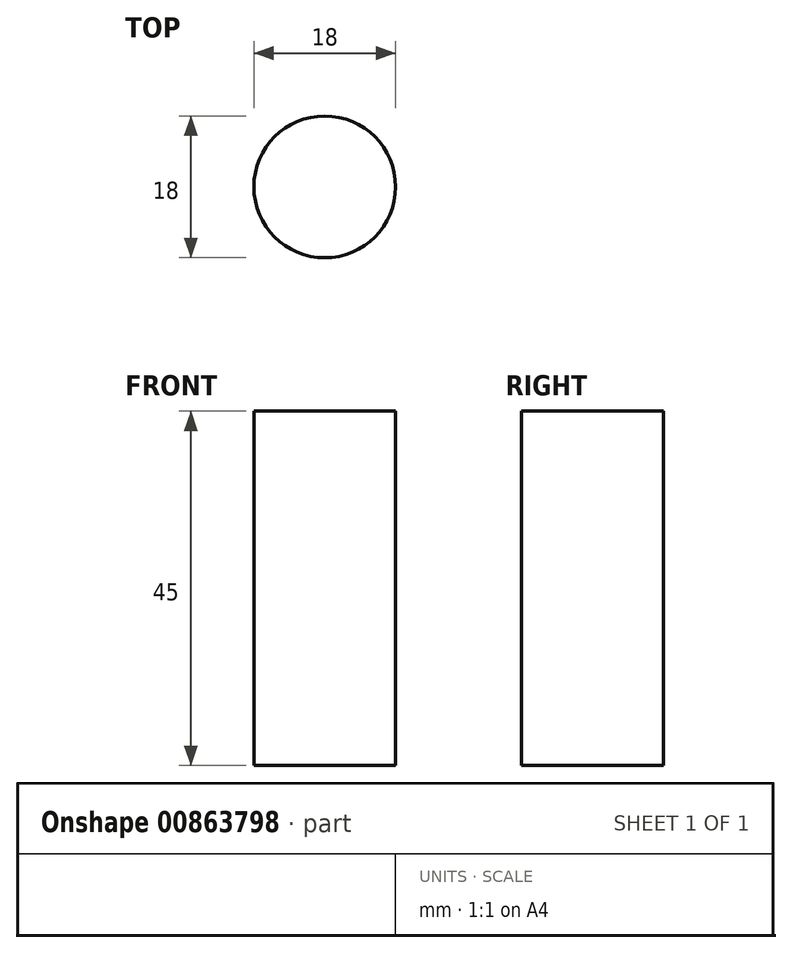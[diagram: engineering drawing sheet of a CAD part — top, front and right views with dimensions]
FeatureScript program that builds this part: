
annotation { "Feature Type Name" : "Feature", "Feature Type Description" : "" }
export const myFeature = defineFeature(function(context is Context, id is Id, definition is map)
    precondition{}
    {
        {
            var Q0;
            Q0=qCreatedBy(makeId("Top.planeOp"),FACE);
            var sketch = newSketch(context, id + "F0", { "sketchPlane" : qUnion([Q0])});
            skCircle(sketch, "E0", {"center": v(0, 0) * mm, "radius": 9 * mm});
            skSolve(sketch);
        }
        {
            var Q0;
            Q0=makeQuery(id+"F0.imprint","IMPRINT",FACE,{"disambiguationData":[TD([[makeQuery(id+"F0.imprint","IMPRINT",EDGE,{"derivedFrom":sQuery(id+"F0.wireOp",EDGE,"E0")}),1.0]])]});
            extrude(context, id + "F1", {"entities" : qUnion([Q0]), "depth" : 45 * mm, "offsetDistance" : 25 * mm});
        }
    });
